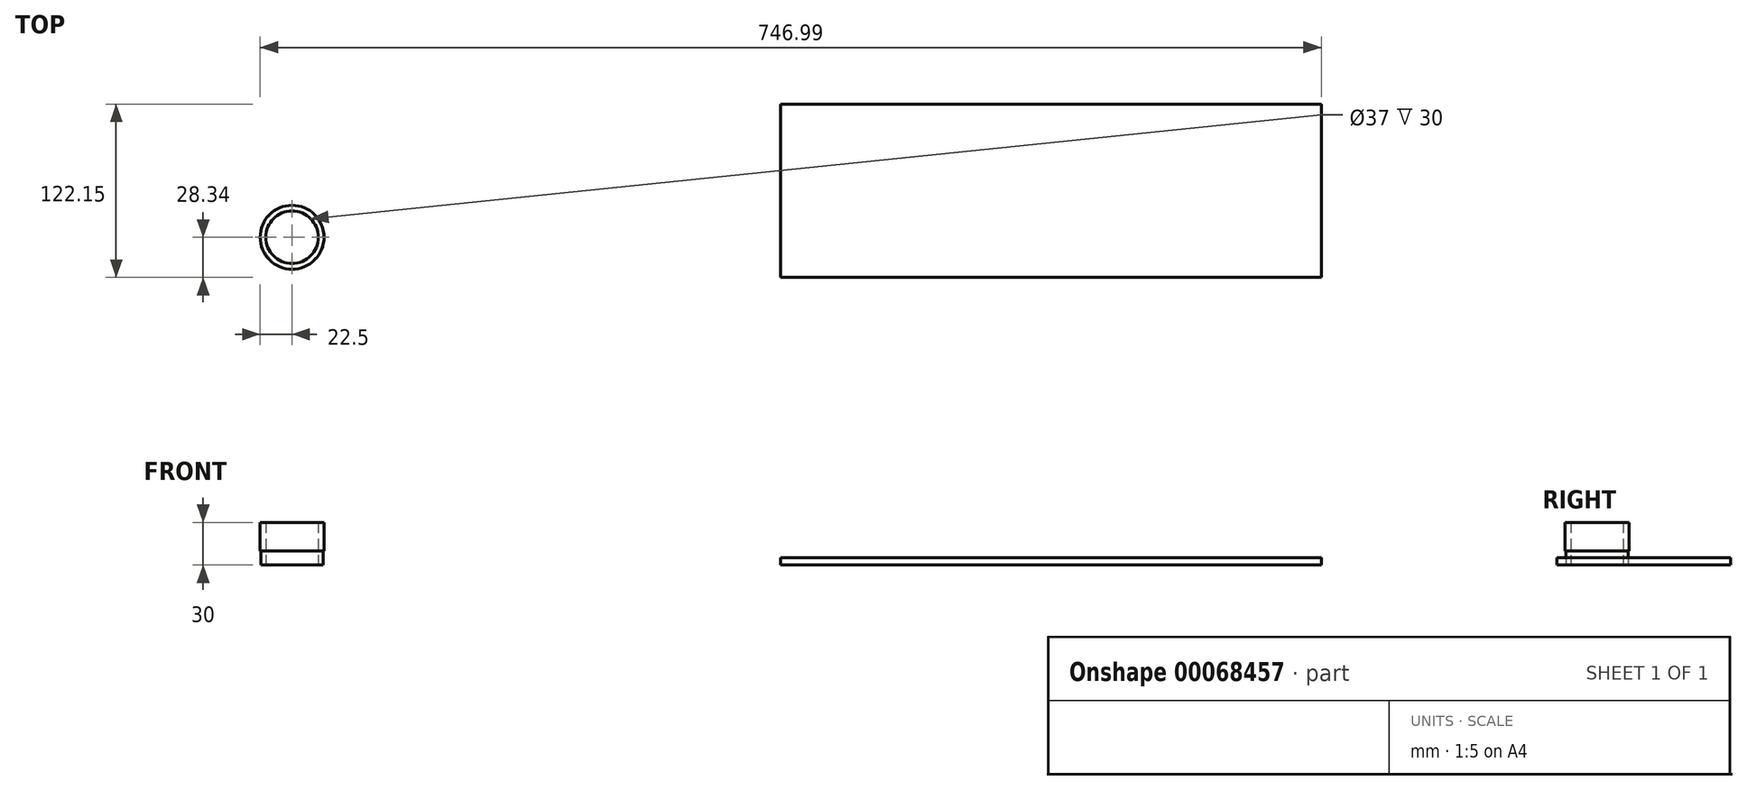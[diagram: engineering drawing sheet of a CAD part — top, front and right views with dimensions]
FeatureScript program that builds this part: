
annotation { "Feature Type Name" : "Feature", "Feature Type Description" : "" }
export const myFeature = defineFeature(function(context is Context, id is Id, definition is map)
    precondition{}
    {
        {
            var Q0;
            Q0=qCreatedBy(makeId("Top.planeOp"),FACE);
            var sketch = newSketch(context, id + "F0", { "sketchPlane" : qUnion([Q0])});
            skCircle(sketch, "E0", {"center": v(0, 0) * mm, "radius": 18.5 * mm});
            skCircle(sketch, "E1", {"center": v(0, 0) * mm, "radius": 22.5 * mm});
            skSolve(sketch);
        }
        {
            var Q0;
            Q0 = qSketchRegion(id + "F0", true);
            extrude(context, id + "F1", {"entities" : qUnion([Q0]), "depth" : 30 * mm});
        }
        {
            var Q0;
            Q0=makeQuery(id+"F1.opExtrude","CAP_FACE",FACE,{"disambiguationData":[OSD([sQuery(id+"F0.wireOp",EDGE,"E0"),sQuery(id+"F0.wireOp",EDGE,"E1")])],"isStart":true});
            var sketch = newSketch(context, id + "F2", { "sketchPlane" : qUnion([Q0])});
            skCircle(sketch, "E2", {"center": v(0, 0) * mm, "radius": 22.5 * mm});
            skCircle(sketch, "E3", {"center": v(0, 0) * mm, "radius": 22 * mm});
            skSolve(sketch);
        }
        {
            var Q0;
            Q0 = qSketchRegion(id + "F2", true);
            extrude(context, id + "F3", {"entities" : qUnion([Q0]), "operationType" : NewBodyOperationType.REMOVE, "oppositeDirection" : true, "depth" : 10 * mm});
        }
        {
            var Q0;
            Q0=qCreatedBy(makeId("Top.planeOp"),FACE);
            var sketch = newSketch(context, id + "F4", { "sketchPlane" : qUnion([Q0])});
            skLineSegment(sketch, "E4.bottom", {"start": v(724.49, -28.34) * mm, "end": v(343.98, -28.34) * mm});
            skLineSegment(sketch, "E4.top", {"start": v(724.49, 93.81) * mm, "end": v(343.98, 93.81) * mm});
            skLineSegment(sketch, "E4.left", {"start": v(724.49, -28.34) * mm, "end": v(724.49, 93.81) * mm});
            skLineSegment(sketch, "E4.right", {"start": v(343.98, -28.34) * mm, "end": v(343.98, 93.81) * mm});
            skSolve(sketch);
        }
        {
            var Q0;
            Q0 = qSketchRegion(id + "F4", true);
            extrude(context, id + "F5", {"entities" : qUnion([Q0]), "depth" : 5 * mm});
        }
        {
            var Q0;
            Q0=makeQuery(id+"F3.boolean.opBoolean","COPY",EDGE,{"derivedFrom":makeQuery(id+"F3.opExtrude","CAP_EDGE",EDGE,{"disambiguationData":[OSD([sQuery(id+"F2.wireOp",EDGE,"E3")])],"isStart":false})});
            fillet(context, id + "F6", {"entities" : qUnion([Q0]), "radius" : 0.4 * mm, "tangentPropagation" : true, "allowEdgeOverflow" : false});
        }
    });
